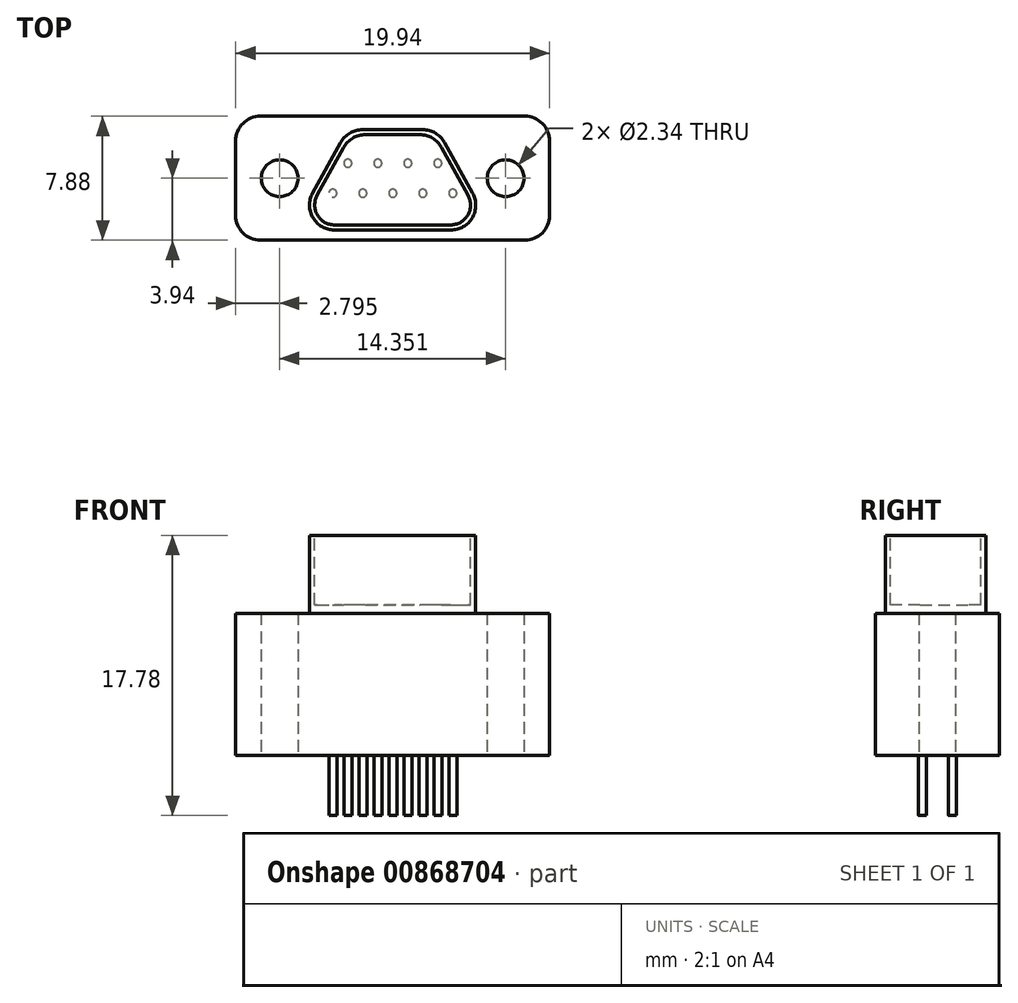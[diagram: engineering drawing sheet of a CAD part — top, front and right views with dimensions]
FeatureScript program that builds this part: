
annotation { "Feature Type Name" : "Feature", "Feature Type Description" : "" }
export const myFeature = defineFeature(function(context is Context, id is Id, definition is map)
    precondition{}
    {
        {
            var Q0;
            Q0=qCreatedBy(makeId("Top.planeOp"),FACE);
            var sketch = newSketch(context, id + "F0", { "sketchPlane" : qUnion([Q0])});
            skLineSegment(sketch, "E0.bottom", {"start": v(-8.4, 3.94) * mm, "end": v(8.4, 3.94) * mm});
            skLineSegment(sketch, "E0.top", {"start": v(-8.4, -3.94) * mm, "end": v(8.4, -3.94) * mm});
            skLineSegment(sketch, "E0.left", {"start": v(-9.97, 2.36) * mm, "end": v(-9.97, -2.36) * mm});
            skLineSegment(sketch, "E0.right", {"start": v(9.97, 2.36) * mm, "end": v(9.97, -2.36) * mm});
            skPoint(sketch, "E0.middle", {"position": v(0, 0) * mm});
            skCircle(sketch, "E1", {"center": v(-7.18, 0) * mm, "radius": 1.17 * mm});
            skCircle(sketch, "E2", {"center": v(7.18, 0) * mm, "radius": 1.17 * mm});
            skPoint(sketch, "E3.visualSharp", {"position": v(-9.97, -3.94) * mm});
            skArc(sketch, "E3.filletArc", {"start": v(-9.97, -2.36) * mm, "mid": v(-9.5, -3.48) * mm, "end": v(-8.4, -3.94) * mm});
            skPoint(sketch, "E4.visualSharp", {"position": v(-9.97, 3.94) * mm});
            skArc(sketch, "E4.filletArc", {"start": v(-8.4, 3.94) * mm, "mid": v(-9.5, 3.48) * mm, "end": v(-9.97, 2.36) * mm});
            skPoint(sketch, "E5.visualSharp", {"position": v(9.97, 3.94) * mm});
            skArc(sketch, "E5.filletArc", {"start": v(9.97, 2.36) * mm, "mid": v(9.5, 3.48) * mm, "end": v(8.4, 3.94) * mm});
            skPoint(sketch, "E6.visualSharp", {"position": v(9.97, -3.94) * mm});
            skArc(sketch, "E6.filletArc", {"start": v(8.4, -3.94) * mm, "mid": v(9.5, -3.48) * mm, "end": v(9.97, -2.36) * mm});
            skSolve(sketch);
        }
        {
            var Q0;
            Q0=makeQuery(id+"F0.imprint","IMPRINT",FACE,{"disambiguationData":[TD([[makeQuery(id+"F0.imprint","IMPRINT",EDGE,{"derivedFrom":sQuery(id+"F0.wireOp",EDGE,"E0.bottom")}),-1.0]])]});
            extrude(context, id + "F1", {"entities" : qUnion([Q0]), "endBound" : BoundingType.SYMMETRIC, "depth" : 9.02 * mm, "offsetDistance" : 25.4 * mm});
        }
        {
            var Q0;
            Q0=makeQuery(id+"F1.opExtrude","CAP_FACE",FACE,{"disambiguationData":[OSD([sQuery(id+"F0.wireOp",EDGE,"E0.bottom"),sQuery(id+"F0.wireOp",EDGE,"E0.top"),sQuery(id+"F0.wireOp",EDGE,"E0.left"),sQuery(id+"F0.wireOp",EDGE,"E0.right"),sQuery(id+"F0.wireOp",EDGE,"E1"),sQuery(id+"F0.wireOp",EDGE,"E2"),sQuery(id+"F0.wireOp",EDGE,"E3.filletArc"),sQuery(id+"F0.wireOp",EDGE,"E4.filletArc"),sQuery(id+"F0.wireOp",EDGE,"E5.filletArc"),sQuery(id+"F0.wireOp",EDGE,"E6.filletArc")])],"isStart":false});
            var sketch = newSketch(context, id + "F2", { "sketchPlane" : qUnion([Q0])});
            skPoint(sketch, "E7.middle", {"position": v(0, 0) * mm});
            skLineSegment(sketch, "E8.top", {"start": v(3.7, -3.29) * mm, "end": v(-3.7, -3.29) * mm});
            skLineSegment(sketch, "E9", {"start": v(-1.91, 3.09) * mm, "end": v(1.92, 3.09) * mm});
            skLineSegment(sketch, "E10", {"start": v(-5.08, -0.95) * mm, "end": v(-3.3, 2.27) * mm});
            skLineSegment(sketch, "E11", {"start": v(3.3, 2.27) * mm, "end": v(5.08, -0.95) * mm});
            skPoint(sketch, "E12.visualSharp", {"position": v(-2.84, 3.09) * mm});
            skArc(sketch, "E12.filletArc", {"start": v(-1.91, 3.09) * mm, "mid": v(-2.71, 2.87) * mm, "end": v(-3.3, 2.27) * mm});
            skPoint(sketch, "E13.visualSharp", {"position": v(-6.38, -3.29) * mm});
            skArc(sketch, "E13.filletArc", {"start": v(-5.08, -0.95) * mm, "mid": v(-5.06, -2.51) * mm, "end": v(-3.7, -3.29) * mm});
            skPoint(sketch, "E14.visualSharp", {"position": v(6.38, -3.29) * mm});
            skArc(sketch, "E14.filletArc", {"start": v(3.7, -3.29) * mm, "mid": v(5.06, -2.51) * mm, "end": v(5.08, -0.95) * mm});
            skPoint(sketch, "E15.visualSharp", {"position": v(2.84, 3.09) * mm});
            skArc(sketch, "E15.filletArc", {"start": v(3.3, 2.27) * mm, "mid": v(2.71, 2.87) * mm, "end": v(1.92, 3.09) * mm});
            skSolve(sketch);
        }
        {
            var Q0;
            Q0=qSketchRegion(id+"F2",true);
            extrude(context, id + "F3", {"entities" : qUnion([Q0]), "operationType" : NewBodyOperationType.ADD, "depth" : 4.95 * mm, "offsetDistance" : 25.4 * mm});
        }
        {
            var Q0;
            Q0=makeQuery(id+"F3.opExtrude","CAP_FACE",FACE,{"disambiguationData":[OSD([sQuery(id+"F2.wireOp",EDGE,"E8.top"),sQuery(id+"F2.wireOp",EDGE,"E9"),sQuery(id+"F2.wireOp",EDGE,"E10"),sQuery(id+"F2.wireOp",EDGE,"E11"),sQuery(id+"F2.wireOp",EDGE,"E12.filletArc"),sQuery(id+"F2.wireOp",EDGE,"E13.filletArc"),sQuery(id+"F2.wireOp",EDGE,"E14.filletArc"),sQuery(id+"F2.wireOp",EDGE,"E15.filletArc")])],"isStart":false});
            var sketch = newSketch(context, id + "F4", { "sketchPlane" : qUnion([Q0])});
            skLineSegment(sketch, "E16", {"start": v(-1.73, 2.77) * mm, "end": v(1.73, 2.77) * mm});
            skLineSegment(sketch, "E17", {"start": v(3.1, 1.96) * mm, "end": v(4.8, -1.09) * mm});
            skLineSegment(sketch, "E18", {"start": v(3.68, -2.97) * mm, "end": v(-3.68, -2.97) * mm});
            skLineSegment(sketch, "E19", {"start": v(-4.8, -1.09) * mm, "end": v(-3.1, 1.96) * mm});
            skPoint(sketch, "E20.visualSharp", {"position": v(-5.84, -2.97) * mm});
            skArc(sketch, "E20.filletArc", {"start": v(-4.8, -1.09) * mm, "mid": v(-4.77, -2.35) * mm, "end": v(-3.68, -2.97) * mm});
            skPoint(sketch, "E21.visualSharp", {"position": v(-2.65, 2.77) * mm});
            skArc(sketch, "E21.filletArc", {"start": v(-1.73, 2.77) * mm, "mid": v(-2.53, 2.55) * mm, "end": v(-3.1, 1.96) * mm});
            skPoint(sketch, "E22.visualSharp", {"position": v(2.66, 2.77) * mm});
            skArc(sketch, "E22.filletArc", {"start": v(3.1, 1.96) * mm, "mid": v(2.53, 2.55) * mm, "end": v(1.73, 2.77) * mm});
            skPoint(sketch, "E23.visualSharp", {"position": v(5.84, -2.97) * mm});
            skArc(sketch, "E23.filletArc", {"start": v(3.68, -2.97) * mm, "mid": v(4.78, -2.35) * mm, "end": v(4.8, -1.09) * mm});
            skSolve(sketch);
        }
        {
            var Q0;
            Q0=qSketchRegion(id+"F4",true);
            extrude(context, id + "F5", {"entities" : qUnion([Q0]), "operationType" : NewBodyOperationType.REMOVE, "depth" : -4.4 * mm, "offsetDistance" : 25.4 * mm});
        }
        {
            var Q0;
            Q0=makeQuery(id+"F1.opExtrude","CAP_FACE",FACE,{"disambiguationData":[OSD([sQuery(id+"F0.wireOp",EDGE,"E0.bottom"),sQuery(id+"F0.wireOp",EDGE,"E0.top"),sQuery(id+"F0.wireOp",EDGE,"E0.left"),sQuery(id+"F0.wireOp",EDGE,"E0.right"),sQuery(id+"F0.wireOp",EDGE,"E1"),sQuery(id+"F0.wireOp",EDGE,"E2"),sQuery(id+"F0.wireOp",EDGE,"E3.filletArc"),sQuery(id+"F0.wireOp",EDGE,"E4.filletArc"),sQuery(id+"F0.wireOp",EDGE,"E5.filletArc"),sQuery(id+"F0.wireOp",EDGE,"E6.filletArc")])],"isStart":true});
            var sketch = newSketch(context, id + "F6", { "sketchPlane" : qUnion([Q0])});
            skCircle(sketch, "E24", {"center": v(-3.8, 0.95) * mm, "radius": 0.25 * mm});
            skCircle(sketch, "E25.1.0.0", {"center": v(-1.9, 0.95) * mm, "radius": 0.25 * mm});
            skCircle(sketch, "E25.2.0.0", {"center": v(0.01, 0.95) * mm, "radius": 0.25 * mm});
            skCircle(sketch, "E25.3.0.0", {"center": v(1.92, 0.95) * mm, "radius": 0.25 * mm});
            skCircle(sketch, "E25.4.0.0", {"center": v(3.82, 0.95) * mm, "radius": 0.25 * mm});
            skLineSegment(sketch, "E25.direction1", {"start": v(-3.8, 0.95) * mm, "end": v(-1.9, 0.95) * mm, "construction": true});
            skCircle(sketch, "E26", {"center": v(-2.84, -0.95) * mm, "radius": 0.25 * mm});
            skCircle(sketch, "E27.1.0.0", {"center": v(-0.94, -0.95) * mm, "radius": 0.25 * mm});
            skCircle(sketch, "E27.2.0.0", {"center": v(0.97, -0.95) * mm, "radius": 0.25 * mm});
            skCircle(sketch, "E27.3.0.0", {"center": v(2.87, -0.95) * mm, "radius": 0.25 * mm});
            skLineSegment(sketch, "E27.direction1", {"start": v(-2.84, -0.95) * mm, "end": v(-0.94, -0.95) * mm, "construction": true});
            skSolve(sketch);
        }
        {
            var Q0;
            Q0=qSketchRegion(id+"F6",true);
            extrude(context, id + "F7", {"entities" : qUnion([Q0]), "operationType" : NewBodyOperationType.ADD, "depth" : 3.8 * mm, "offsetDistance" : 25.4 * mm});
        }
    });
